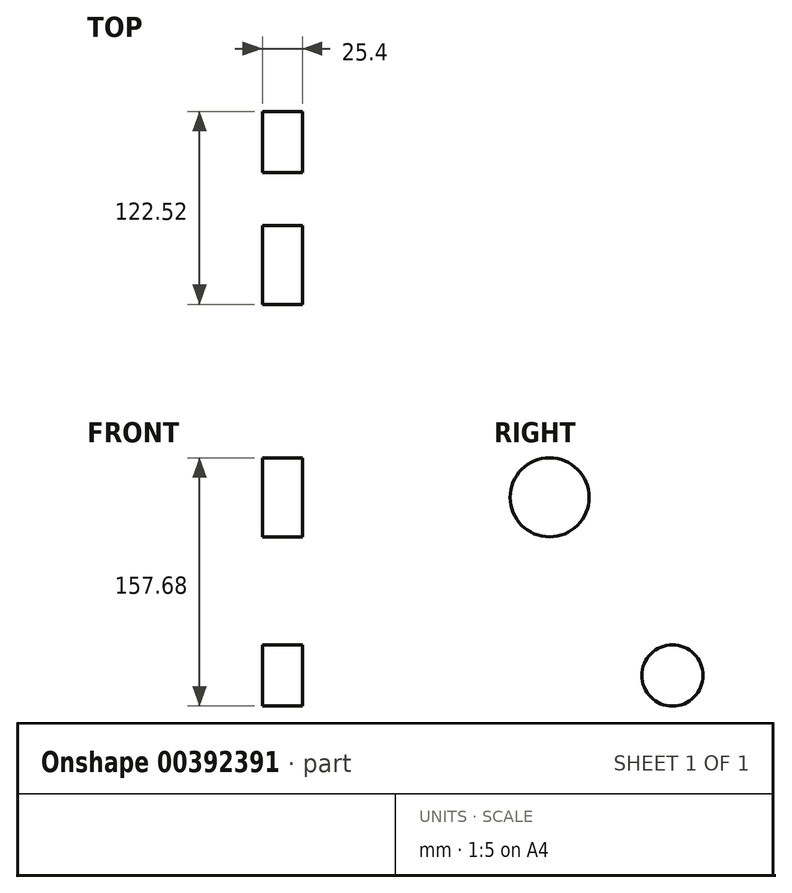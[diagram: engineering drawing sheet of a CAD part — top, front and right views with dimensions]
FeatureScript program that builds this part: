
annotation { "Feature Type Name" : "Feature", "Feature Type Description" : "" }
export const myFeature = defineFeature(function(context is Context, id is Id, definition is map)
    precondition{}
    {
        {
            var Q0;
            Q0=qCreatedBy(makeId("Right.planeOp"),FACE);
            var sketch = newSketch(context, id + "F0", { "sketchPlane" : qUnion([Q0])});
            skCircle(sketch, "E0", {"center": v(0, 0) * mm, "radius": 25.08 * mm});
            skCircle(sketch, "E1", {"center": v(78, -113.16) * mm, "radius": 19.44 * mm});
            skCircle(sketch, "E2", {"center": v(-57.65, -170.04) * mm, "radius": 20.55 * mm});
            skArc(sketch, "E3", {"start": v(-28.14, -304.7) * mm, "mid": v(-30.22, -419.57) * mm, "end": v(77.68, -380.1) * mm});
            skLineSegment(sketch, "E4", {"start": v(0, 0) * mm, "end": v(78, -113.16) * mm});
            skLineSegment(sketch, "E5", {"start": v(-57.65, -170.04) * mm, "end": v(78, -113.16) * mm});
            skArc(sketch, "E6", {"start": v(-32.34, -298.32) * mm, "mid": v(-34.66, -425.8) * mm, "end": v(85.08, -382) * mm});
            skLineSegment(sketch, "E7", {"start": v(-28.14, -304.7) * mm, "end": v(10.2, -362.85) * mm});
            skLineSegment(sketch, "E8", {"start": v(77.68, -380.1) * mm, "end": v(10.2, -362.85) * mm});
            skArc(sketch, "E9", {"start": v(-32.34, -298.32) * mm, "mid": v(-16.71, -269.34) * mm, "end": v(-32.27, -240.32) * mm});
            skArc(sketch, "E10", {"start": v(-28.14, -304.7) * mm, "mid": v(-9.07, -269.35) * mm, "end": v(-28.04, -233.95) * mm});
            skLineSegment(sketch, "E11", {"start": v(-32.34, -298.32) * mm, "end": v(-51.48, -269.3) * mm});
            skLineSegment(sketch, "E12", {"start": v(-32.27, -240.32) * mm, "end": v(-51.48, -269.3) * mm});
            skSolve(sketch);
        }
        {
            var Q0;
            {var subQ0=sQuery(id+"F0.wireOp",EDGE,"E4");var subQ1=sQuery(id+"F0.wireOp",EDGE,"E1");var subQ2=makeQuery(id+"F0.imprint","INTERSECT",VERTEX,{"derivedFrom":[subQ1,subQ0]});Q0=makeQuery(id+"F0.imprint","IMPRINT",FACE,{"disambiguationData":[TD([[makeQuery(id+"F0.imprint","IMPRINT",EDGE,{"disambiguationData":[TD([[subQ2,-1.0]])],"derivedFrom":subQ1}),1.0]])]});}
            var Q1;
            Q1=makeQuery(id+"F0.imprint","IMPRINT",FACE,{"disambiguationData":[TD([[makeQuery(id+"F0.imprint","IMPRINT",EDGE,{"derivedFrom":sQuery(id+"F0.wireOp",EDGE,"E0")}),1.0]])]});
            var Q2;
            {var subQ0=sQuery(id+"F0.wireOp",EDGE,"E4");var subQ1=sQuery(id+"F0.wireOp",EDGE,"E1");var subQ2=makeQuery(id+"F0.imprint","INTERSECT",VERTEX,{"derivedFrom":[subQ1,subQ0]});Q2=makeQuery(id+"F0.imprint","IMPRINT",FACE,{"disambiguationData":[TD([[makeQuery(id+"F0.imprint","IMPRINT",EDGE,{"disambiguationData":[TD([[subQ2,1.0]])],"derivedFrom":subQ1}),1.0]])]});}
            var Q3;
            Q3=sQuery(id+"F0.wireOp",EDGE,"E1");
            extrude(context, id + "F1", {"entities" : qUnion([Q0, Q1, Q2]), "surfaceEntities" : qUnion([Q3]), "depth" : 25.4 * mm});
        }
    });
